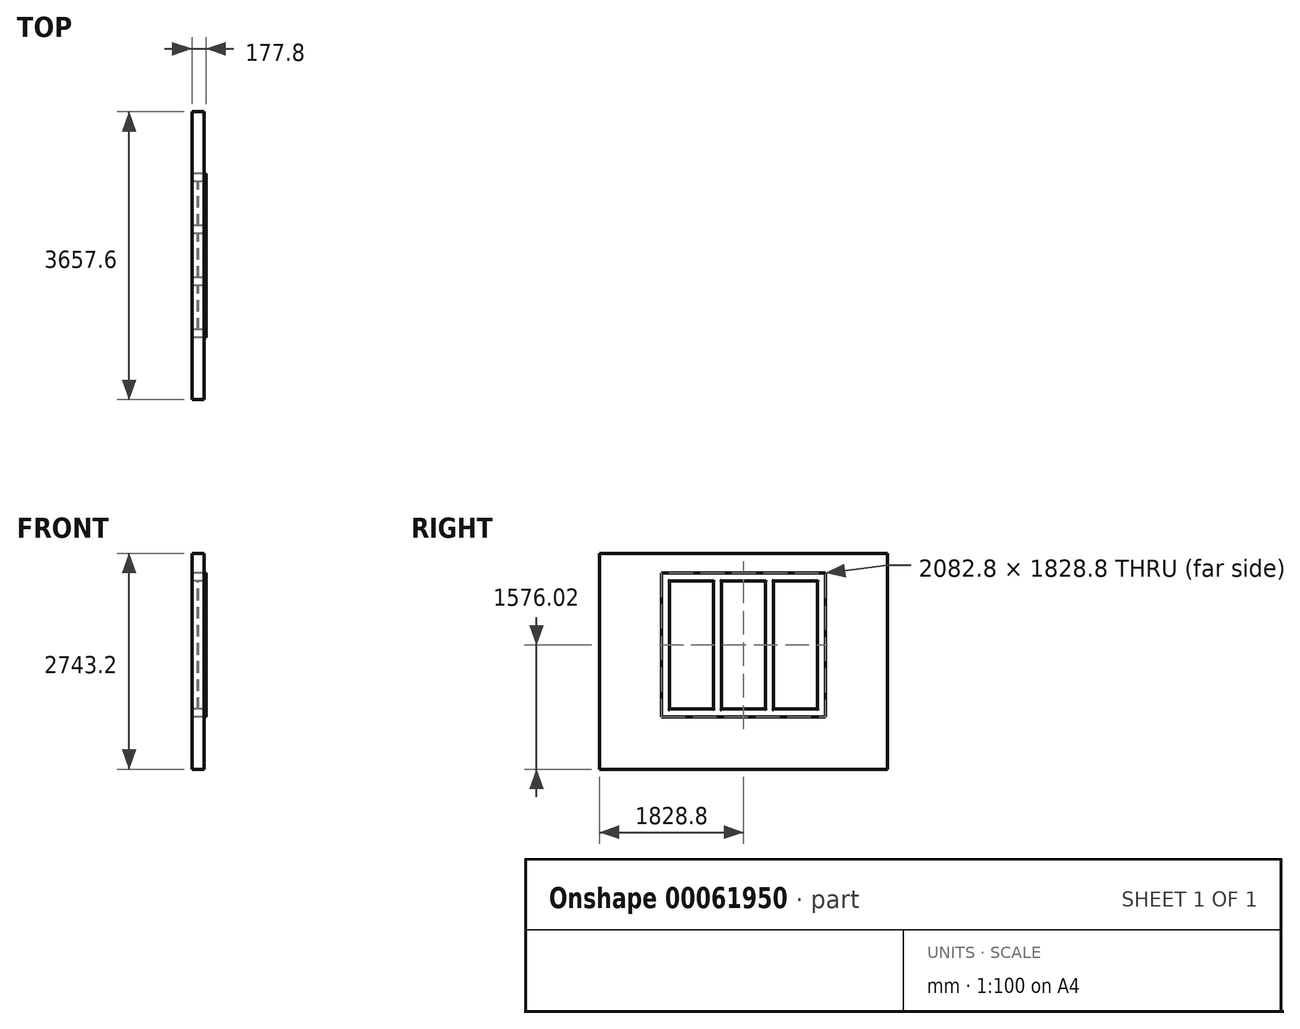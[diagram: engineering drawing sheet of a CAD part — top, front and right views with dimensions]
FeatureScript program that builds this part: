
annotation { "Feature Type Name" : "Feature", "Feature Type Description" : "" }
export const myFeature = defineFeature(function(context is Context, id is Id, definition is map)
    precondition{}
    {
        {
            var Q0;
            Q0=qCreatedBy(makeId("Right.planeOp"),FACE);
            var sketch = newSketch(context, id + "F0", { "sketchPlane" : qUnion([Q0])});
            skLineSegment(sketch, "E0.rect.bottom", {"start": v(1828.8, -1371.6) * mm, "end": v(-1828.8, -1371.6) * mm});
            skLineSegment(sketch, "E0.rect.top", {"start": v(1828.8, 1371.6) * mm, "end": v(-1828.8, 1371.6) * mm});
            skLineSegment(sketch, "E0.rect.left", {"start": v(1828.8, -1371.6) * mm, "end": v(1828.8, 1371.6) * mm});
            skLineSegment(sketch, "E0.rect.right", {"start": v(-1828.8, -1371.6) * mm, "end": v(-1828.8, 1371.6) * mm});
            skPoint(sketch, "E0.rect.middle", {"position": v(0, 0) * mm});
            skLineSegment(sketch, "E1.top", {"start": v(-279.4, 1118.81) * mm, "end": v(279.4, 1118.81) * mm});
            skLineSegment(sketch, "E1.left", {"start": v(-279.4, -608.39) * mm, "end": v(-279.4, 1017.21) * mm});
            skLineSegment(sketch, "E1.right", {"start": v(279.4, -608.39) * mm, "end": v(279.4, 1017.21) * mm});
            skLineSegment(sketch, "E2", {"start": v(-279.4, -709.99) * mm, "end": v(279.4, -709.99) * mm});
            skLineSegment(sketch, "E3", {"start": v(0, 1371.6) * mm, "end": v(0, 1118.81) * mm, "construction": true});
            skLineSegment(sketch, "E4.bottom", {"start": v(279.4, -709.99) * mm, "end": v(381, -709.99) * mm});
            skLineSegment(sketch, "E4.top", {"start": v(279.4, 1118.81) * mm, "end": v(381, 1118.81) * mm});
            skLineSegment(sketch, "E4.right", {"start": v(381, -608.39) * mm, "end": v(381, 1017.21) * mm});
            skLineSegment(sketch, "E5.bottom", {"start": v(-279.4, -709.99) * mm, "end": v(-381, -709.99) * mm});
            skLineSegment(sketch, "E5.top", {"start": v(-279.4, 1118.81) * mm, "end": v(-381, 1118.81) * mm});
            skLineSegment(sketch, "E5.right", {"start": v(-381, -608.39) * mm, "end": v(-381, 1017.21) * mm});
            skLineSegment(sketch, "E6", {"start": v(330.2, 1118.81) * mm, "end": v(330.2, -709.99) * mm, "construction": true});
            skLineSegment(sketch, "E7", {"start": v(-330.2, -709.99) * mm, "end": v(-330.2, 1118.81) * mm, "construction": true});
            skLineSegment(sketch, "E8.MirrorCS", {"start": v(939.8, -608.39) * mm, "end": v(939.8, 1017.21) * mm});
            skLineSegment(sketch, "E9.MirrorCS", {"start": v(1041.4, -709.99) * mm, "end": v(1041.4, 1118.81) * mm});
            skLineSegment(sketch, "E10.MirrorCS", {"start": v(939.8, 1118.81) * mm, "end": v(1041.4, 1118.81) * mm});
            skLineSegment(sketch, "E11.MirrorCS", {"start": v(939.8, 1118.81) * mm, "end": v(381, 1118.81) * mm});
            skLineSegment(sketch, "E12.MirrorCS", {"start": v(939.8, -709.99) * mm, "end": v(1041.4, -709.99) * mm});
            skLineSegment(sketch, "E13.MirrorCS", {"start": v(939.8, -709.99) * mm, "end": v(381, -709.99) * mm});
            skLineSegment(sketch, "E14.MirrorCS", {"start": v(-381, 1118.81) * mm, "end": v(-939.8, 1118.81) * mm});
            skLineSegment(sketch, "E15.MirrorCS", {"start": v(-381, -709.99) * mm, "end": v(-939.8, -709.99) * mm});
            skLineSegment(sketch, "E16.MirrorCS", {"start": v(-939.8, -608.39) * mm, "end": v(-939.8, 1017.21) * mm});
            skLineSegment(sketch, "E17.MirrorCS", {"start": v(-1041.4, -709.99) * mm, "end": v(-1041.4, 1118.81) * mm});
            skLineSegment(sketch, "E18.MirrorCS", {"start": v(-939.8, -709.99) * mm, "end": v(-1041.4, -709.99) * mm});
            skLineSegment(sketch, "E19.MirrorCS", {"start": v(-939.8, 1118.81) * mm, "end": v(-1041.4, 1118.81) * mm});
            skLineSegment(sketch, "E20.bottom", {"start": v(-1041.4, 1118.81) * mm, "end": v(1041.4, 1118.81) * mm});
            skLineSegment(sketch, "E20.top", {"start": v(-939.8, 1017.21) * mm, "end": v(-381, 1017.21) * mm});
            skLineSegment(sketch, "E20.left", {"start": v(-1041.4, 1118.81) * mm, "end": v(-1041.4, 1017.21) * mm});
            skLineSegment(sketch, "E20.right", {"start": v(1041.4, 1118.81) * mm, "end": v(1041.4, 1017.21) * mm});
            skLineSegment(sketch, "E21.bottom", {"start": v(-1041.4, -709.99) * mm, "end": v(1041.4, -709.99) * mm});
            skLineSegment(sketch, "E21.top", {"start": v(-939.8, -608.39) * mm, "end": v(-381, -608.39) * mm});
            skLineSegment(sketch, "E21.left", {"start": v(-1041.4, -709.99) * mm, "end": v(-1041.4, -608.39) * mm});
            skLineSegment(sketch, "E21.right", {"start": v(1041.4, -709.99) * mm, "end": v(1041.4, -608.39) * mm});
            skPoint(sketch, "E22.orphan", {"position": v(-939.8, 1118.81) * mm});
            skPoint(sketch, "E23.orphan", {"position": v(939.8, 1118.81) * mm});
            skPoint(sketch, "E24.orphan", {"position": v(939.8, -709.99) * mm});
            skPoint(sketch, "E25.orphan", {"position": v(-939.8, -709.99) * mm});
            skLineSegment(sketch, "E26.trimOffspring", {"start": v(-279.4, -608.39) * mm, "end": v(279.4, -608.39) * mm});
            skLineSegment(sketch, "E27.trimOffspring", {"start": v(381, -608.39) * mm, "end": v(939.8, -608.39) * mm});
            skLineSegment(sketch, "E28.trimOffspring", {"start": v(381, 1017.21) * mm, "end": v(939.8, 1017.21) * mm});
            skLineSegment(sketch, "E29.trimOffspring", {"start": v(-279.4, 1017.21) * mm, "end": v(279.4, 1017.21) * mm});
            skSolve(sketch);
        }
        {
            var Q0;
            Q0=makeQuery(id+"F0.imprint","IMPRINT",FACE,{"disambiguationData":[TD([[makeQuery(id+"F0.imprint","IMPRINT",EDGE,{"derivedFrom":sQuery(id+"F0.wireOp",EDGE,"E0.rect.bottom")}),-1.0]])]});
            var Q1;
            Q1=makeQuery(id+"F0.imprint","IMPRINT",FACE,{"disambiguationData":[TD([[makeQuery(id+"F0.imprint","IMPRINT",EDGE,{"derivedFrom":sQuery(id+"F0.wireOp",EDGE,"E0.rect.top")}),-1.0]])]});
            extrude(context, id + "F1", {"entities" : qUnion([Q0, Q1]), "depth" : 152.4 * mm});
        }
        {
            var Q0;
            Q0=makeQuery(id+"F0.imprint","IMPRINT",FACE,{"disambiguationData":[TD([[makeQuery(id+"F0.imprint","IMPRINT",EDGE,{"derivedFrom":sQuery(id+"F0.wireOp",EDGE,"E1.right")}),-1.0]])]});
            extrude(context, id + "F2", {"entities" : qUnion([Q0]), "depth" : 177.8 * mm});
        }
        {
            var Q0;
            {var subQ0=sQuery(id+"F0.wireOp",EDGE,"E21.top");var subQ1=sQuery(id+"F0.wireOp",EDGE,"E5.right");var subQ2=makeQuery(id+"F0.imprint","INTERSECT",VERTEX,{"derivedFrom":[subQ1,subQ0]});Q0=makeQuery(id+"F0.imprint","IMPRINT",FACE,{"disambiguationData":[TD([[makeQuery(id+"F0.imprint","IMPRINT",EDGE,{"disambiguationData":[TD([[subQ2,-1.0]])],"derivedFrom":subQ1}),1.0]])]});}
            var Q1;
            {var subQ0=sQuery(id+"F0.wireOp",EDGE,"E21.top");var subQ1=sQuery(id+"F0.wireOp",EDGE,"E1.right");var subQ2=makeQuery(id+"F0.imprint","INTERSECT",VERTEX,{"derivedFrom":[subQ1,subQ0]});Q1=makeQuery(id+"F0.imprint","IMPRINT",FACE,{"disambiguationData":[TD([[makeQuery(id+"F0.imprint","IMPRINT",EDGE,{"disambiguationData":[TD([[subQ2,-1.0]])],"derivedFrom":subQ1}),1.0]])]});}
            var Q2;
            {var subQ0=sQuery(id+"F0.wireOp",EDGE,"E21.top");var subQ1=sQuery(id+"F0.wireOp",EDGE,"E4.right");var subQ2=makeQuery(id+"F0.imprint","INTERSECT",VERTEX,{"derivedFrom":[subQ1,subQ0]});Q2=makeQuery(id+"F0.imprint","IMPRINT",FACE,{"disambiguationData":[TD([[makeQuery(id+"F0.imprint","IMPRINT",EDGE,{"disambiguationData":[TD([[subQ2,-1.0]])],"derivedFrom":subQ1}),-1.0]])]});}
            extrude(context, id + "F3", {"entities" : qUnion([Q0, Q1, Q2]), "endBound" : BoundingType.SYMMETRIC, "depth" : 12.7 * mm});
        }
        {
            var Q0;
            Q0=makeQuery(id+"F3.opExtrude","SWEPT_BODY",BODY,{"disambiguationData":[OSD([sQuery(id+"F0.wireOp",EDGE,"E5.right"),sQuery(id+"F0.wireOp",EDGE,"E16.MirrorCS"),sQuery(id+"F0.wireOp",EDGE,"E20.top"),sQuery(id+"F0.wireOp",EDGE,"E21.top")])]});
            var Q1;
            Q1=makeQuery(id+"F3.opExtrude","SWEPT_BODY",BODY,{"disambiguationData":[OSD([sQuery(id+"F0.wireOp",EDGE,"E1.right"),sQuery(id+"F0.wireOp",EDGE,"E1.left"),sQuery(id+"F0.wireOp",EDGE,"E20.top"),sQuery(id+"F0.wireOp",EDGE,"E21.top")])]});
            var Q2;
            Q2=makeQuery(id+"F3.opExtrude","SWEPT_BODY",BODY,{"disambiguationData":[OSD([sQuery(id+"F0.wireOp",EDGE,"E4.right"),sQuery(id+"F0.wireOp",EDGE,"E8.MirrorCS"),sQuery(id+"F0.wireOp",EDGE,"E20.top"),sQuery(id+"F0.wireOp",EDGE,"E21.top")])]});
            transform(context, id + "F4", {"entities" : qUnion([Q0, Q1, Q2]), "transformType" : TransformType.TRANSLATION_3D, "dx" : 76.2 * mm, "dy" : 0 * mm, "dz" : 0 * mm, "makeCopy" : false});
        }
        {
            var Q0;
            Q0=makeQuery(id+"F2.opExtrude","CAP_EDGE",EDGE,{"disambiguationData":[OSD([sQuery(id+"F0.wireOp",EDGE,"E16.MirrorCS")])],"isStart":false});
            var Q1;
            Q1=makeQuery(id+"F2.opExtrude","CAP_EDGE",EDGE,{"disambiguationData":[OSD([sQuery(id+"F0.wireOp",EDGE,"E20.top")])],"isStart":false});
            var Q2;
            Q2=makeQuery(id+"F2.opExtrude","CAP_EDGE",EDGE,{"disambiguationData":[OSD([sQuery(id+"F0.wireOp",EDGE,"E5.right")])],"isStart":false});
            var Q3;
            Q3=makeQuery(id+"F2.opExtrude","CAP_EDGE",EDGE,{"disambiguationData":[OSD([sQuery(id+"F0.wireOp",EDGE,"E29.trimOffspring")])],"isStart":false});
            var Q4;
            Q4=makeQuery(id+"F2.opExtrude","CAP_EDGE",EDGE,{"disambiguationData":[OSD([sQuery(id+"F0.wireOp",EDGE,"E1.left")])],"isStart":false});
            var Q5;
            Q5=makeQuery(id+"F2.opExtrude","CAP_EDGE",EDGE,{"disambiguationData":[OSD([sQuery(id+"F0.wireOp",EDGE,"E1.right")])],"isStart":false});
            var Q6;
            Q6=makeQuery(id+"F2.opExtrude","CAP_EDGE",EDGE,{"disambiguationData":[OSD([sQuery(id+"F0.wireOp",EDGE,"E21.top")])],"isStart":false});
            var Q7;
            Q7=makeQuery(id+"F2.opExtrude","CAP_EDGE",EDGE,{"disambiguationData":[OSD([sQuery(id+"F0.wireOp",EDGE,"E26.trimOffspring")])],"isStart":false});
            var Q8;
            Q8=makeQuery(id+"F2.opExtrude","CAP_EDGE",EDGE,{"disambiguationData":[OSD([sQuery(id+"F0.wireOp",EDGE,"E27.trimOffspring")])],"isStart":false});
            var Q9;
            Q9=makeQuery(id+"F2.opExtrude","CAP_EDGE",EDGE,{"disambiguationData":[OSD([sQuery(id+"F0.wireOp",EDGE,"E8.MirrorCS")])],"isStart":false});
            var Q10;
            Q10=makeQuery(id+"F2.opExtrude","CAP_EDGE",EDGE,{"disambiguationData":[OSD([sQuery(id+"F0.wireOp",EDGE,"E4.right")])],"isStart":false});
            var Q11;
            Q11=makeQuery(id+"F2.opExtrude","CAP_EDGE",EDGE,{"disambiguationData":[OSD([sQuery(id+"F0.wireOp",EDGE,"E28.trimOffspring")])],"isStart":false});
            fillet(context, id + "F5", {"entities" : qUnion([Q0, Q1, Q2, Q3, Q4, Q5, Q6, Q7, Q8, Q9, Q10, Q11]), "radius" : 9.52 * mm, "tangentPropagation" : true, "allowEdgeOverflow" : false});
        }
    });
